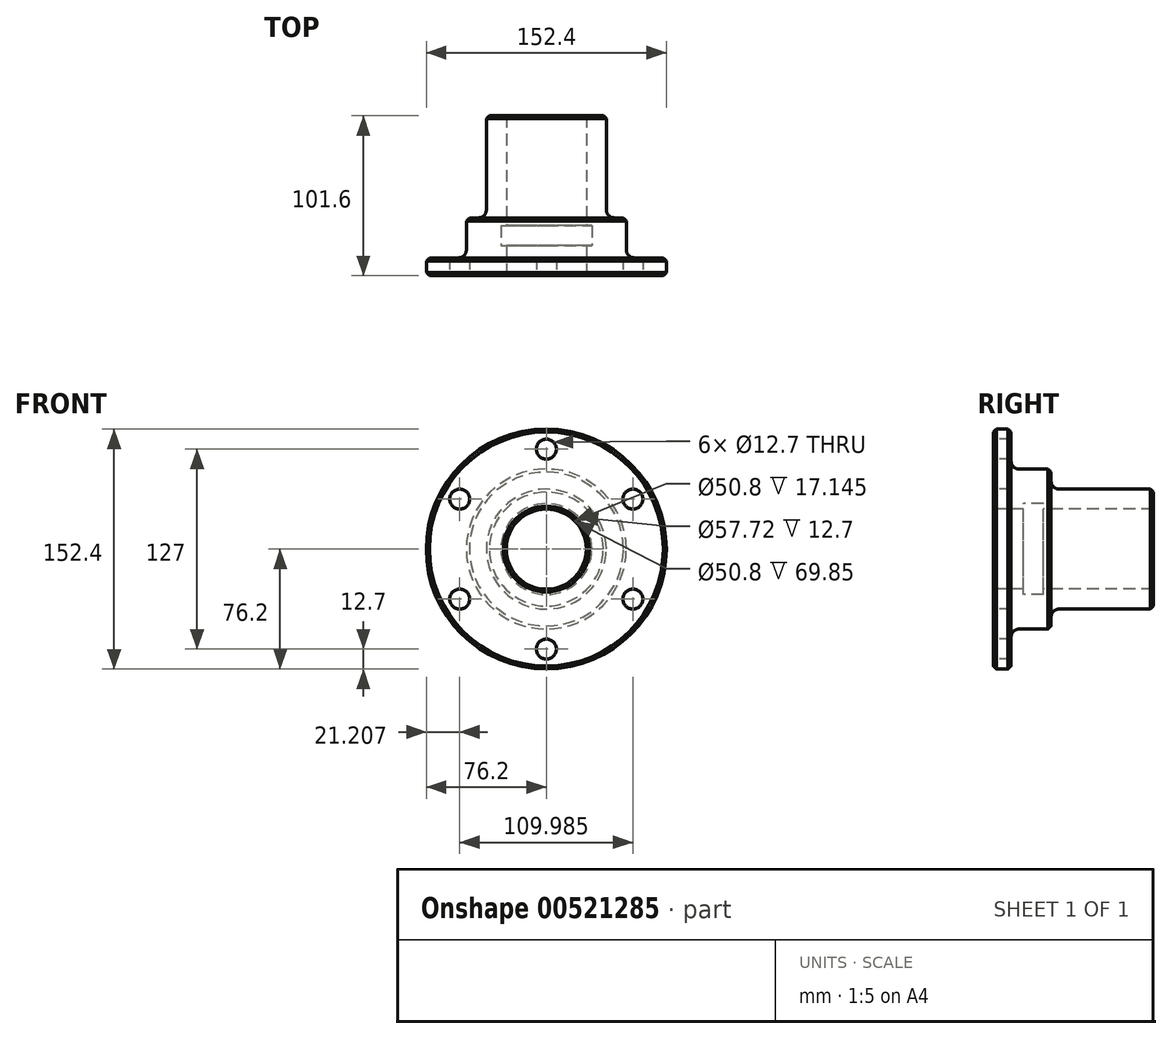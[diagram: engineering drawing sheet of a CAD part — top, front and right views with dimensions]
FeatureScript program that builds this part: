
annotation { "Feature Type Name" : "Feature", "Feature Type Description" : "" }
export const myFeature = defineFeature(function(context is Context, id is Id, definition is map)
    precondition{}
    {
        {
            var Q0;
            Q0=qCreatedBy(makeId("Right.planeOp"),FACE);
            var sketch = newSketch(context, id + "F0", { "sketchPlane" : qUnion([Q0])});
            skLineSegment(sketch, "E0", {"start": v(-44.53, 0) * mm, "end": v(76.71, 0) * mm});
            skLineSegment(sketch, "E1", {"start": v(-44.53, 25.4) * mm, "end": v(-44.53, 76.2) * mm});
            skLineSegment(sketch, "E2.0", {"start": v(-33.22, 50.8) * mm, "end": v(-33.22, 76.2) * mm});
            skLineSegment(sketch, "E3.0", {"start": v(-7.82, 38.1) * mm, "end": v(-7.82, 50.8) * mm});
            skLineSegment(sketch, "E4.0", {"start": v(-44.53, 25.4) * mm, "end": v(-25.48, 25.4) * mm});
            skLineSegment(sketch, "E5.0", {"start": v(-33.22, 50.8) * mm, "end": v(-7.82, 50.8) * mm});
            skLineSegment(sketch, "E6.0", {"start": v(-44.53, 76.2) * mm, "end": v(-33.22, 76.2) * mm});
            skLineSegment(sketch, "E7.0", {"start": v(-46.15, 38.1) * mm, "end": v(-44.53, 38.1) * mm});
            skLineSegment(sketch, "E8", {"start": v(57.07, 25.4) * mm, "end": v(57.07, 38.1) * mm});
            skLineSegment(sketch, "E9.trimOffspring", {"start": v(-7.82, 38.1) * mm, "end": v(57.07, 38.1) * mm});
            skLineSegment(sketch, "E10", {"start": v(-25.48, 25.4) * mm, "end": v(-25.48, 28.86) * mm});
            skLineSegment(sketch, "E11", {"start": v(-25.48, 28.86) * mm, "end": v(-12.78, 28.86) * mm});
            skLineSegment(sketch, "E12", {"start": v(-12.78, 28.86) * mm, "end": v(-12.78, 25.4) * mm});
            skLineSegment(sketch, "E13.trimOffspring", {"start": v(-12.78, 25.4) * mm, "end": v(57.07, 25.4) * mm});
            skSolve(sketch);
        }
        {
            var Q0;
            Q0=makeQuery(id+"F0.imprint","IMPRINT",FACE,{"disambiguationData":[TD([[makeQuery(id+"F0.imprint","IMPRINT",EDGE,{"derivedFrom":sQuery(id+"F0.wireOp",EDGE,"E2.0")}),1.0]])]});
            var Q1;
            Q1=sQuery(id+"F0.wireOp",EDGE,"E0");
            revolve(context, id + "F1", {"entities" : qUnion([Q0]), "axis" : qUnion([Q1]), "revolveType" : RevolveType.FULL});
        }
        {
            var Q0;
            Q0=qCreatedBy(makeId("Top.planeOp"),FACE);
            cPlane(context, id + "F2", {"entities" : qUnion([Q0]), "cplaneType" : CPlaneType.OFFSET, "offset" : 49.53 * mm, "width" : 152.4 * mm, "height" : 152.4 * mm});
        }
        {
            var Q0;
            Q0=makeQuery(id+"F1.opRevolve","SWEPT_EDGE",EDGE,{"disambiguationData":[OSD([sQuery(id+"F0.wireOp",EDGE,"E1"),sQuery(id+"F0.wireOp",EDGE,"E6.0")])]});
            var Q1;
            Q1=makeQuery(id+"F1.opRevolve","SWEPT_EDGE",EDGE,{"disambiguationData":[OSD([sQuery(id+"F0.wireOp",EDGE,"E2.0"),sQuery(id+"F0.wireOp",EDGE,"E6.0")])]});
            var Q2;
            Q2=makeQuery(id+"F1.opRevolve","SWEPT_EDGE",EDGE,{"disambiguationData":[OSD([sQuery(id+"F0.wireOp",EDGE,"E3.0"),sQuery(id+"F0.wireOp",EDGE,"E5.0")])]});
            var Q3;
            Q3=makeQuery(id+"F1.opRevolve","SWEPT_EDGE",EDGE,{"disambiguationData":[OSD([sQuery(id+"F0.wireOp",EDGE,"E8"),sQuery(id+"F0.wireOp",EDGE,"E9.trimOffspring")])]});
            var Q4;
            Q4=makeQuery(id+"F1.opRevolve","SWEPT_EDGE",EDGE,{"disambiguationData":[OSD([sQuery(id+"F0.wireOp",EDGE,"E1"),sQuery(id+"F0.wireOp",EDGE,"E4.0")])]});
            chamfer(context, id + "F3", {"entities" : qUnion([Q0, Q1, Q2, Q3, Q4]), "width" : 1.9 * mm, "tangentPropagation" : true});
        }
        {
            var Q0;
            Q0=makeQuery(id+"F1.opRevolve","SWEPT_EDGE",EDGE,{"disambiguationData":[OSD([sQuery(id+"F0.wireOp",EDGE,"E2.0"),sQuery(id+"F0.wireOp",EDGE,"E5.0")])]});
            var Q1;
            Q1=makeQuery(id+"F1.opRevolve","SWEPT_EDGE",EDGE,{"disambiguationData":[OSD([sQuery(id+"F0.wireOp",EDGE,"E3.0"),sQuery(id+"F0.wireOp",EDGE,"E9.trimOffspring")])]});
            fillet(context, id + "F4", {"entities" : qUnion([Q0, Q1]), "radius" : 5.08 * mm, "tangentPropagation" : true, "allowEdgeOverflow" : false});
        }
        {
            var Q0;
            Q0=makeQuery(id+"F1.opRevolve","SWEPT_FACE",FACE,{"disambiguationData":[OSD([sQuery(id+"F0.wireOp",EDGE,"E1")])]});
            var sketch = newSketch(context, id + "F5", { "sketchPlane" : qUnion([Q0])});
            skCircle(sketch, "E14", {"center": v(0, 0) * mm, "radius": 63.5 * mm, "construction": true});
            skCircle(sketch, "E15", {"center": v(0, 63.5) * mm, "radius": 6.35 * mm});
            skCircle(sketch, "E16.1.0", {"center": v(-55, 31.75) * mm, "radius": 6.35 * mm});
            skCircle(sketch, "E16.2.0", {"center": v(-55, -31.75) * mm, "radius": 6.35 * mm});
            skCircle(sketch, "E16.3.0", {"center": v(0, -63.5) * mm, "radius": 6.35 * mm});
            skCircle(sketch, "E16.4.0", {"center": v(55, -31.75) * mm, "radius": 6.35 * mm});
            skCircle(sketch, "E16.5.0", {"center": v(55, 31.75) * mm, "radius": 6.35 * mm});
            skSolve(sketch);
        }
        {
            var Q0;
            Q0=makeQuery(id+"F5.imprint","IMPRINT",FACE,{"disambiguationData":[TD([[makeQuery(id+"F5.imprint","IMPRINT",EDGE,{"derivedFrom":sQuery(id+"F5.wireOp",EDGE,"E16.1.0")}),1.0]])]});
            var Q1;
            Q1=makeQuery(id+"F5.imprint","IMPRINT",FACE,{"disambiguationData":[TD([[makeQuery(id+"F5.imprint","IMPRINT",EDGE,{"derivedFrom":sQuery(id+"F5.wireOp",EDGE,"E16.2.0")}),1.0]])]});
            var Q2;
            Q2=makeQuery(id+"F5.imprint","IMPRINT",FACE,{"disambiguationData":[TD([[makeQuery(id+"F5.imprint","IMPRINT",EDGE,{"derivedFrom":sQuery(id+"F5.wireOp",EDGE,"E16.3.0")}),1.0]])]});
            var Q3;
            Q3=makeQuery(id+"F5.imprint","IMPRINT",FACE,{"disambiguationData":[TD([[makeQuery(id+"F5.imprint","IMPRINT",EDGE,{"derivedFrom":sQuery(id+"F5.wireOp",EDGE,"E16.4.0")}),1.0]])]});
            var Q4;
            Q4=makeQuery(id+"F5.imprint","IMPRINT",FACE,{"disambiguationData":[TD([[makeQuery(id+"F5.imprint","IMPRINT",EDGE,{"derivedFrom":sQuery(id+"F5.wireOp",EDGE,"E16.5.0")}),1.0]])]});
            var Q5;
            Q5=makeQuery(id+"F5.imprint","IMPRINT",FACE,{"disambiguationData":[TD([[makeQuery(id+"F5.imprint","IMPRINT",EDGE,{"derivedFrom":sQuery(id+"F5.wireOp",EDGE,"E15")}),1.0]])]});
            var Q6;
            Q6=sQuery(id+"F5.wireOp",EDGE,"E16.1.0");
            var Q7;
            Q7=sQuery(id+"F5.wireOp",EDGE,"E16.2.0");
            var Q8;
            Q8=sQuery(id+"F5.wireOp",EDGE,"E16.3.0");
            var Q9;
            Q9=sQuery(id+"F5.wireOp",EDGE,"E16.4.0");
            var Q10;
            Q10=sQuery(id+"F5.wireOp",EDGE,"E16.5.0");
            var Q11;
            Q11=sQuery(id+"F5.wireOp",EDGE,"E15");
            extrude(context, id + "F6", {"entities" : qUnion([Q0, Q1, Q2, Q3, Q4, Q5]), "operationType" : NewBodyOperationType.REMOVE, "surfaceEntities" : qUnion([Q6, Q7, Q8, Q9, Q10, Q11]), "oppositeDirection" : true, "depth" : 15.88 * mm, "offsetDistance" : 25.4 * mm});
        }
    });
